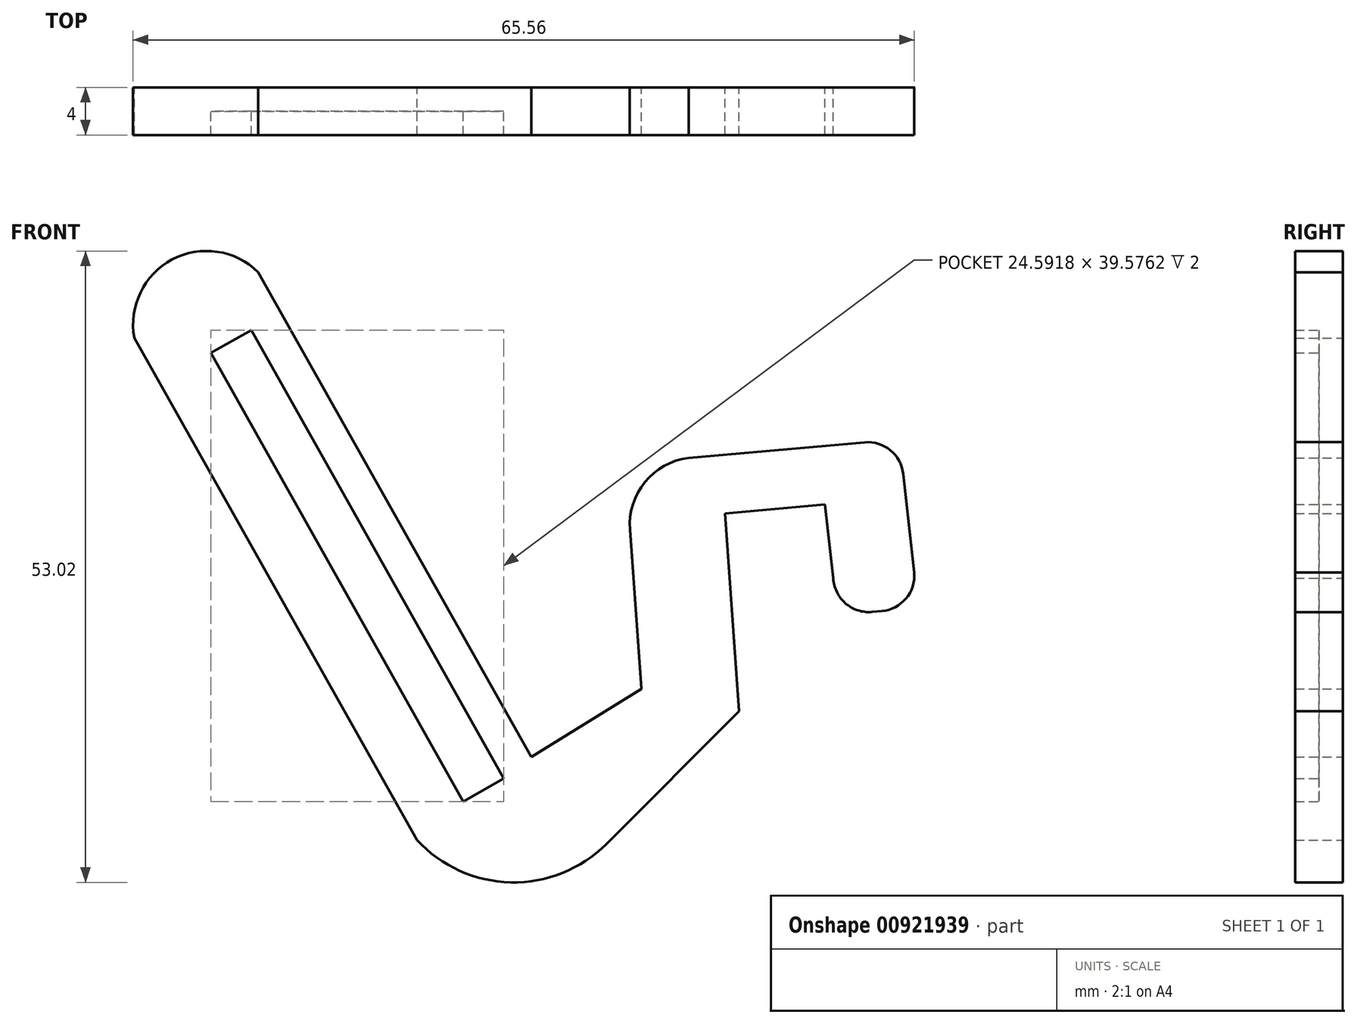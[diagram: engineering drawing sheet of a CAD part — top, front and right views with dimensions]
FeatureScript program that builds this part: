
annotation { "Feature Type Name" : "Feature", "Feature Type Description" : "" }
export const myFeature = defineFeature(function(context is Context, id is Id, definition is map)
    precondition{}
    {
        {
            var Q0;
            Q0=qCreatedBy(makeId("Front.planeOp"),FACE);
            var sketch = newSketch(context, id + "F0", { "sketchPlane" : qUnion([Q0])});
            skLineSegment(sketch, "E0.filletArc", {"start": v(24.58, 49.74) * mm, "end": v(24.58, 49.74) * mm});
            skLineSegment(sketch, "E1.filletArc", {"start": v(27.2, 46.46) * mm, "end": v(27.2, 46.46) * mm});
            skLineSegment(sketch, "E2.filletArc", {"start": v(32.4, 46.46) * mm, "end": v(32.4, 46.46) * mm});
            skPoint(sketch, "E3.endSnap0", {"position": v(-48.4, 44.46) * mm});
            skPoint(sketch, "E4.visualSharp", {"position": v(-12.8, 44.46) * mm});
            skArc(sketch, "E4.filletArc", {"start": v(-45.74, 44.59) * mm, "mid": v(-45.73, 44.6) * mm, "end": v(-45.73, 44.6) * mm});
            skLineSegment(sketch, "E5.filletArc", {"start": v(-12.65, 38.15) * mm, "end": v(-12.65, 38.15) * mm});
            skArc(sketch, "E6.MirrorCS", {"start": v(-43.07, 44.59) * mm, "mid": v(-43.07, 44.6) * mm, "end": v(-43.07, 44.6) * mm});
            skLineSegment(sketch, "E7.MirrorCS", {"start": v(-9.13, 3.2) * mm, "end": v(-9.37, 2.71) * mm});
            skLineSegment(sketch, "E8.MirrorCS", {"start": v(22.7, 24.15) * mm, "end": v(21.89, 24.08) * mm});
            skLineSegment(sketch, "E9.MirrorCS", {"start": v(-12.43, 8.17) * mm, "end": v(-9.03, 10.08) * mm});
            skArc(sketch, "E10.MirrorCS", {"start": v(25.42, 27.4) * mm, "mid": v(24.73, 25.2) * mm, "end": v(22.7, 24.15) * mm});
            skArc(sketch, "E11.MirrorCS", {"start": v(21.89, 24.08) * mm, "mid": v(19.65, 24.8) * mm, "end": v(18.63, 26.91) * mm});
            skLineSegment(sketch, "E12.MirrorCS", {"start": v(-30.22, 47.74) * mm, "end": v(-33.62, 45.83) * mm});
            skArc(sketch, "E13.MirrorCS", {"start": v(1.56, 31) * mm, "mid": v(2.83, 34.99) * mm, "end": v(6.48, 37.02) * mm});
            skArc(sketch, "E14.MirrorCS", {"start": v(21.25, 38.32) * mm, "mid": v(23.42, 37.66) * mm, "end": v(24.5, 35.67) * mm});
            skLineSegment(sketch, "E15.MirrorCS", {"start": v(9.55, 32.36) * mm, "end": v(17.94, 33.1) * mm});
            skPoint(sketch, "E16.MirrorP", {"position": v(-43, 44.46) * mm});
            skPoint(sketch, "E17.MirrorP", {"position": v(-37.8, 44.46) * mm});
            skLineSegment(sketch, "E18.MirrorCS", {"start": v(17.94, 33.1) * mm, "end": v(18.63, 26.91) * mm});
            skPoint(sketch, "E19.MirrorP", {"position": v(-40.4, 44.46) * mm});
            skLineSegment(sketch, "E20.MirrorCS", {"start": v(21.25, 38.32) * mm, "end": v(6.48, 37.02) * mm});
            skLineSegment(sketch, "E21.MirrorCS", {"start": v(2.51, 17.6) * mm, "end": v(-6.72, 11.9) * mm});
            skPoint(sketch, "E22.MirrorP", {"position": v(2.63, 36.9) * mm});
            skLineSegment(sketch, "E23.MirrorCS", {"start": v(-33.62, 45.83) * mm, "end": v(-12.43, 8.17) * mm});
            skPoint(sketch, "E24.MirrorP", {"position": v(-10.46, 36.58) * mm});
            skPoint(sketch, "E25.MirrorP", {"position": v(10.73, 23.35) * mm});
            skPoint(sketch, "E26.MirrorP", {"position": v(24.17, 38.58) * mm});
            skPoint(sketch, "E27.MirrorP", {"position": v(25.7, 24.15) * mm});
            skLineSegment(sketch, "E28.MirrorCS", {"start": v(9.55, 32.36) * mm, "end": v(10.73, 15.73) * mm});
            skLineSegment(sketch, "E29.MirrorCS", {"start": v(10.73, 15.73) * mm, "end": v(-0.44, 4.58) * mm});
            skLineSegment(sketch, "E30.MirrorCS", {"start": v(25.42, 27.4) * mm, "end": v(24.5, 35.67) * mm});
            skArc(sketch, "E31.MirrorCS", {"start": v(-40.02, 47.09) * mm, "mid": v(-36.86, 53.67) * mm, "end": v(-29.64, 52.61) * mm});
            skLineSegment(sketch, "E32.MirrorCS", {"start": v(-40.02, 47.09) * mm, "end": v(-16.3, 4.93) * mm});
            skLineSegment(sketch, "E33.MirrorCS", {"start": v(-6.72, 11.9) * mm, "end": v(-29.64, 52.61) * mm});
            skArc(sketch, "E34.MirrorCS", {"start": v(-0.44, 4.58) * mm, "mid": v(-8.44, 1.37) * mm, "end": v(-16.3, 4.93) * mm});
            skLineSegment(sketch, "E35.MirrorCS", {"start": v(-9.03, 10.08) * mm, "end": v(-30.22, 47.74) * mm});
            skLineSegment(sketch, "E36.MirrorCS", {"start": v(1.56, 31) * mm, "end": v(2.51, 17.6) * mm});
            skPoint(sketch, "E37.MirrorP", {"position": v(-33.33, 44.46) * mm});
            skPoint(sketch, "E38.MirrorP", {"position": v(12.05, 32.56) * mm});
            skSolve(sketch);
        }
        {
            var Q0;
            Q0=makeQuery(id+"F0.imprint","IMPRINT",FACE,{"disambiguationData":[TD([[makeQuery(id+"F0.imprint","IMPRINT",EDGE,{"derivedFrom":sQuery(id+"F0.wireOp",EDGE,"ok77M1no-juQo-zo8L-mibJ-HDuDLWQOTgjE")}),1.0]])]});
            var Q1;
            Q1=makeQuery(id+"F0.imprint","IMPRINT",FACE,{"disambiguationData":[TD([[makeQuery(id+"F0.imprint","IMPRINT",EDGE,{"derivedFrom":sQuery(id+"F0.wireOp",EDGE,"E8.MirrorCS")}),-1.0]])]});
            extrude(context, id + "F1", {"entities" : qUnion([Q0, Q1]), "depth" : 4 * mm, "offsetDistance" : 25 * mm});
        }
        {
            var Q0;
            Q0=makeQuery(id+"F0.imprint","IMPRINT",FACE,{"disambiguationData":[TD([[makeQuery(id+"F0.imprint","IMPRINT",EDGE,{"derivedFrom":sQuery(id+"F0.wireOp",EDGE,"E9.MirrorCS")}),1.0]])]});
            extrude(context, id + "F2", {"entities" : qUnion([Q0]), "operationType" : NewBodyOperationType.ADD, "depth" : 2 * mm, "offsetDistance" : 25 * mm});
        }
    });
